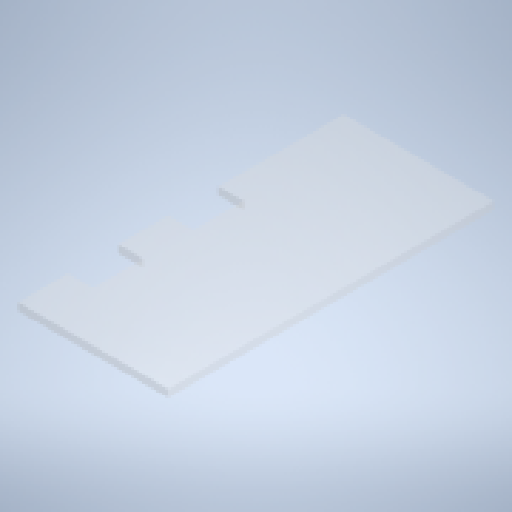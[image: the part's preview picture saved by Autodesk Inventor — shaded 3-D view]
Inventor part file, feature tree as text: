
AUTODESK INVENTOR PART (.ipt)
format: ipt  version: 2024 (Build 280153000, 153)  size: 156,672 bytes
history: native  units: mm
features: extrude x2, sketch x2, other x1
ambient origin geometry x8: Origin, YZ Plane, XZ Plane, XY Plane, X Axis, Y Axis, Z Axis, Center Point
bodies: Body1 (feature_tree)
feature tree (5):
  other  "솔리드1"
  extrude  "돌출1"  Depth=130.0mm
  extrude  "돌출2"  Depth=60.0mm
  sketch  "스케치1"
  sketch  "스케치2"
